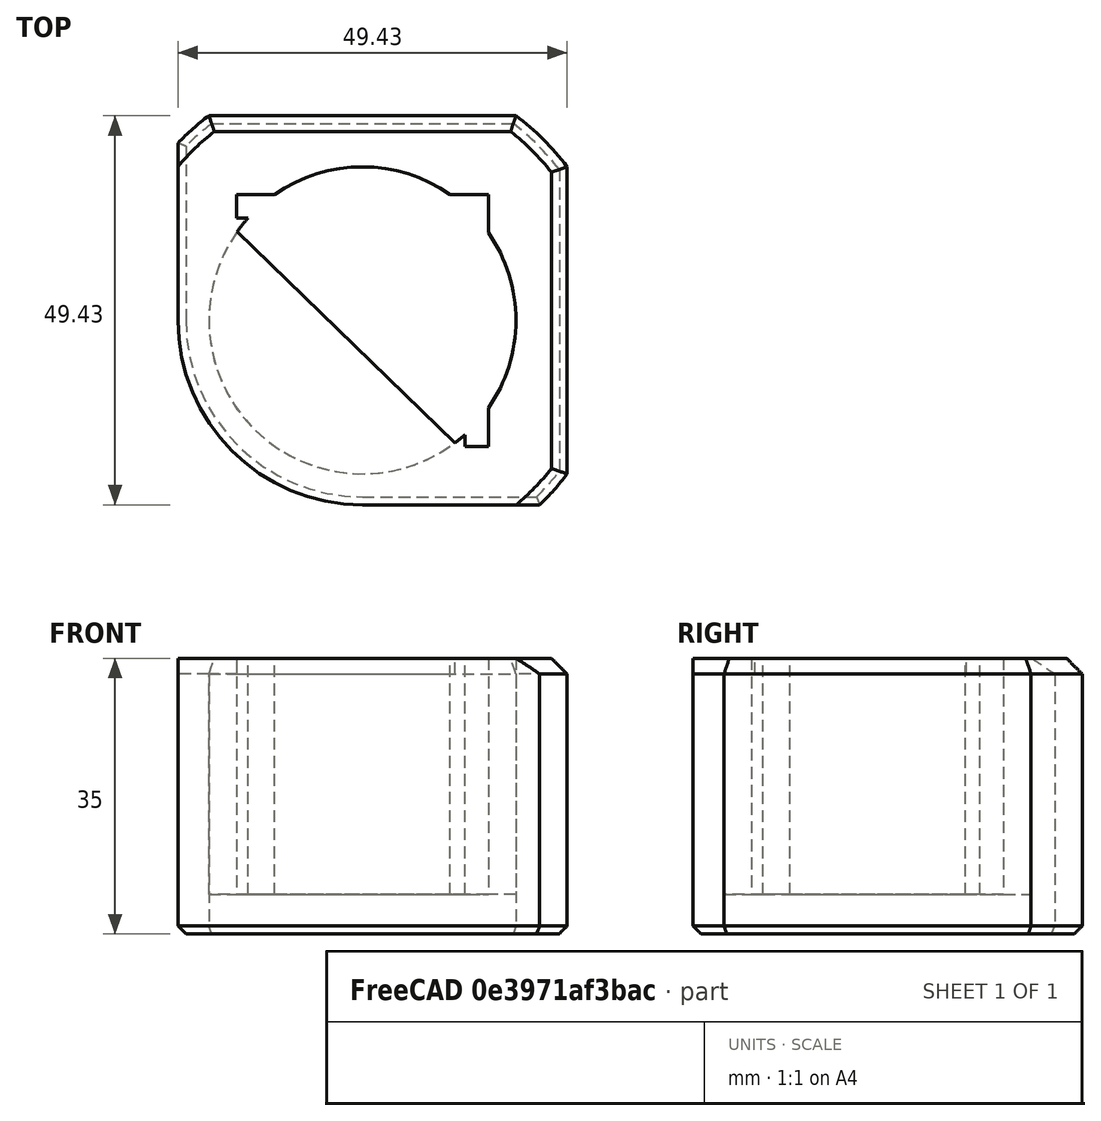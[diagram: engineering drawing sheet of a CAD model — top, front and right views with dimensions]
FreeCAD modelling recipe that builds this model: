
FCSTD DOCUMENT  (FreeCAD 0.19R)
Label: tankfeetRC1
License: All rights reserved
LicenseURL: http://en.wikipedia.org/wiki/All_rights_reserved
objects: Sketcher::SketchObject×6, PartDesign::Pocket×4, PartDesign::Pad×2, PartDesign::Chamfer×2, PartDesign::Body×1, Mesh::Feature×1
note: 23 computed .brp shape members not serialized (recipe doc carries the construction recipe); baked Part::Feature solids carry a one-line shape summary decoded from their .brp

FEATURE [Sketcher::SketchObject] Sketch
  FullyConstrained = true
  MapMode = 5
  Support = -> [XY_Plane]
  sketch-geometry (1):
    g0: Circle CenterX=0 CenterY=0 CenterZ=0 NormalX=0 NormalY=0 NormalZ=1 AngleXU=0 Radius=32.5
  constraints (2):
    c: Coincident(g0,g-1)
    c: Diameter(g0) = 65
FEATURE [PartDesign::Pad] Pad
  Direction = (1,1,1)
  Length = 35
  Length2 = 100
  Profile = -> Sketch
  Type = 0
FEATURE [Sketcher::SketchObject] Sketch001
  FullyConstrained = true
  MapMode = 5
  Placement = pos=(0,0,35) rot=(0,0,1;0rad)
  Support = -> [Pad]
  sketch-geometry (10):
    g0: LineSegment StartX=-16 StartY=16 StartZ=0 EndX=16 EndY=16 EndZ=0
    g1: LineSegment StartX=16 StartY=16 StartZ=0 EndX=16 EndY=-16 EndZ=0
    g2: LineSegment StartX=16 StartY=-16 StartZ=0 EndX=-16 EndY=-16 EndZ=0
    g3: LineSegment StartX=-16 StartY=-16 StartZ=0 EndX=-16 EndY=16 EndZ=0
    g4: LineSegment StartX=-16 StartY=16 StartZ=0 EndX=16 EndY=16 EndZ=0
    g5: LineSegment StartX=16 StartY=16 StartZ=0 EndX=16 EndY=-16 EndZ=0
    g6: LineSegment StartX=16 StartY=-16 StartZ=0 EndX=13 EndY=-16 EndZ=0
    g7: LineSegment StartX=13 StartY=-16 StartZ=0 EndX=13 EndY=13 EndZ=0
    g8: LineSegment StartX=13 StartY=13 StartZ=0 EndX=-16 EndY=13 EndZ=0
    g9: LineSegment StartX=-16 StartY=13 StartZ=0 EndX=-16 EndY=16 EndZ=0
  constraints (27):
    c: Coincident(g0,g1)
    c: Coincident(g1,g2)
    c: Coincident(g2,g3)
    c: Coincident(g3,g0)
    c: Horizontal(g0)
    c: Horizontal(g2)
    c: Vertical(g1)
    c: Vertical(g3)
    c: Symmetric(g1,g0,g-1)
    c: Distance(g0) = 32
    c: Equal(g1,g0)
    c: Coincident(g4,g5)
    c: Coincident(g5,g6)
    c: Coincident(g6,g7)
    c: Vertical(g7)
    c: Coincident(g7,g8)
    c: Horizontal(g8)
    c: Coincident(g8,g9)
    c: Coincident(g9,g4)
    c: Vertical(g9)
    c: Distance(g9) = 3
    c: Equal(g6,g9)
    c: Horizontal(g6)
    c: Symmetric(g4,g4,g-2)
    c: Symmetric(g5,g4,g-1)
    c: Distance(g4) = 32
    c: Equal(g5,g4)
FEATURE [PartDesign::Pocket] Pocket
  BaseFeature = -> Pad
  Length = 30
  Length2 = 100
  Profile = -> Sketch001
  Type = 0
FEATURE [Sketcher::SketchObject] Sketch002
  FullyConstrained = true
  MapMode = 5
  Placement = pos=(0,0,35) rot=(0,0,1;0rad)
  Support = -> [Pocket]
  sketch-geometry (1):
    g0: Circle CenterX=0 CenterY=0 CenterZ=0 NormalX=0 NormalY=0 NormalZ=1 AngleXU=0 Radius=19.5
  constraints (2):
    c: Coincident(g0,g-1)
    c: Diameter(g0) = 39
FEATURE [PartDesign::Pocket] Pocket001
  BaseFeature = -> Pocket
  Length = 30
  Length2 = 100
  Profile = -> Sketch002
  Type = 0
FEATURE [Sketcher::SketchObject] Sketch003
  FullyConstrained = false
  MapMode = 5
  Placement = pos=(0,0,35) rot=(0,0,1;0rad)
  Support = -> [Pocket001]
  sketch-geometry (10):
    g0: LineSegment StartX=26 StartY=26 StartZ=0 EndX=26 EndY=-26 EndZ=0
    g1: LineSegment StartX=26 StartY=-26 StartZ=0 EndX=67.4944 EndY=-26 EndZ=0
    g2: LineSegment StartX=67.4944 StartY=-26 StartZ=0 EndX=72.3472 EndY=49.8195 EndZ=0
    g3: LineSegment StartX=72.3472 StartY=49.8195 StartZ=0 EndX=-56.3282 EndY=49.8195 EndZ=0
    g4: LineSegment StartX=-56.3282 StartY=49.8195 StartZ=0 EndX=-56.3282 EndY=-44.3399 EndZ=0
    g5: LineSegment StartX=-56.3282 StartY=-44.3399 StartZ=0 EndX=22.1064 EndY=-44.3399 EndZ=0
    g6: LineSegment StartX=22.1064 StartY=-44.3399 StartZ=0 EndX=27.22 EndY=-26 EndZ=0
    g7: LineSegment StartX=27.22 StartY=-26 StartZ=0 EndX=-26 EndY=-26 EndZ=0
    g8: LineSegment StartX=-26 StartY=-26 StartZ=0 EndX=-26 EndY=26 EndZ=0
    g9: LineSegment StartX=-26 StartY=26 StartZ=0 EndX=26 EndY=26 EndZ=0
  constraints (22):
    c: Vertical(g0)
    c: Coincident(g0,g1)
    c: Horizontal(g1)
    c: Coincident(g1,g2)
    c: Coincident(g2,g3)
    c: Horizontal(g3)
    c: Coincident(g3,g4)
    c: Vertical(g4)
    c: Coincident(g4,g5)
    c: Horizontal(g5)
    c: Coincident(g5,g6)
    c: Coincident(g6,g7)
    c: Horizontal(g7)
    c: Coincident(g7,g8)
    c: Coincident(g8,g9)
    c: Coincident(g9,g0)
    c: Symmetric(g0,g8,g-2)
    c: Symmetric(g8,g7,g-1)
    c: Distance(g8) = 52
    c: Distance(g9) = 52
    c: Distance(g0) = 52
    c: Distance(g7) = 53.22
FEATURE [PartDesign::Pocket] Pocket002
  BaseFeature = -> Pocket001
  Length = 5
  Length2 = 100
  Profile = -> Sketch003
  Type = 1
FEATURE [Sketcher::SketchObject] Sketch004
  FullyConstrained = false
  MapMode = 5
  Placement = pos=(0,0,35) rot=(0,0,1;0rad)
  Support = -> [Pocket002]
  sketch-geometry (2):
    g0: ArcOfCircle CenterX=0 CenterY=0 CenterZ=0 NormalX=0 NormalY=0 NormalZ=1 AngleXU=0 Radius=22.0943 StartAngle=2.50673 EndAngle=5.37592
    g1: LineSegment StartX=-17.7893 StartY=13.1034 StartZ=0 EndX=13.6079 EndY=-17.4064 EndZ=0
  constraints (4):
    c: Coincident(g0,g-1)
    c: Coincident(g1,g0)
    c: Coincident(g1,g0)
    c: Distance(g0,g1) = 3
FEATURE [PartDesign::Pad] Pad001
  BaseFeature = -> Pocket002
  Direction = (1,1,1)
  Length = 2
  Length2 = 100
  Profile = -> Sketch004
  Reversed = true
  Type = 0
FEATURE [Sketcher::SketchObject] Sketch005
  FullyConstrained = false
  MapMode = 5
  Placement = pos=(0,0,35) rot=(0,0,1;0rad)
  Support = -> [Pad001]
  sketch-geometry (5):
    g0: ArcOfCircle CenterX=0 CenterY=0 CenterZ=0 NormalX=0 NormalY=0 NormalZ=1 AngleXU=0 Radius=23.4313 StartAngle=3.14159 EndAngle=4.71239
    g1: LineSegment StartX=-23.4313 StartY=2.9e-15 StartZ=0 EndX=-23.4313 EndY=32.6981 EndZ=0
    g2: LineSegment StartX=-23.4313 StartY=32.6981 StartZ=0 EndX=-71.4663 EndY=-64.3554 EndZ=0
    g3: LineSegment StartX=-4.3e-15 StartY=-23.4313 StartZ=0 EndX=33.6024 EndY=-23.4313 EndZ=0
    g4: LineSegment StartX=33.6024 StartY=-23.4313 StartZ=0 EndX=-71.4663 EndY=-64.3554 EndZ=0
  constraints (8):
    c: Coincident(g0,g-1)
    c: PointOnObject(g0,g-1)
    c: PointOnObject(g0,g-2)
    c: Tangent(g0,g1) = 1.5708
    c: Coincident(g1,g2)
    c: Tangent(g0,g3) = -1.5708
    c: Coincident(g3,g4)
    c: Coincident(g4,g2)
FEATURE [PartDesign::Pocket] Pocket003
  BaseFeature = -> Pad001
  Length = 5
  Length2 = 100
  Profile = -> Sketch005
  Type = 1
FEATURE [PartDesign::Chamfer] Chamfer
  Angle = 45
  Base = -> Pocket003 [Edge12,Edge19,Edge3,Edge14,Edge15]
  BaseFeature = -> Pocket003
  ChamferType = 0
  FlipDirection = false
  Size = 2
  Size2 = 1
  SupportTransform = false
FEATURE [PartDesign::Chamfer] Chamfer001
  Angle = 45
  Base = -> Chamfer [Face4]
  BaseFeature = -> Chamfer
  ChamferType = 0
  FlipDirection = false
  Size = 1
  Size2 = 1
  SupportTransform = false
FEATURE [PartDesign::Body] Body
  Group = -> [Sketch,Pad,Sketch001,Pocket,Sketch002,Pocket001,Sketch003,Pocket002,Sketch004,Pad001,Sketch005,Pocket003,Chamfer,Chamfer001]
  Origin = -> Origin
  Tip = -> Chamfer001
FEATURE [Mesh::Feature] Mesh  label="Chamfer001 (Meshed)"
